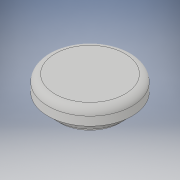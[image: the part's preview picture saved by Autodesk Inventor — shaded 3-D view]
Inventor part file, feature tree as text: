
AUTODESK INVENTOR PART (.ipt)
format: ipt  version: 2017 (Build 210142000, 142)  size: 125,440 bytes
history: native  units: in
note: dims shown in document units (in); Inventor stores cm internally (conversion verified against a paired STEP export)
features: revolve x1, chamfer x1, sketch x1
ambient origin geometry x8: Origin, YZ Plane, XZ Plane, XY Plane, X Axis, Y Axis, Z Axis, Center Point
bodies: Solid1 (feature_tree)
feature tree (3):
  revolve  "Revolution1"  [1 undecoded]
  chamfer  "Chamfer1"  Distance=0.75in
  sketch  "Sketch1"  dims[d0=0.59in d1=0.22in d2=0.75in d3=0.5in d4=0.125in d5=90.0deg d6=0.0625in d7=0.125in d8=45.0deg]
note: 1 required parameter value undecoded (feature->parameter linkage not recoverable at this tier; creation-order binding heuristic only, values carry confidence <= 0.55)
